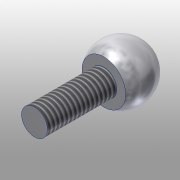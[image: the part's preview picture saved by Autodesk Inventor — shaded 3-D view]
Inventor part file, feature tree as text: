
AUTODESK INVENTOR PART (.ipt)
format: ipt  version: 2015 (Build 190159000, 159)  size: 129,024 bytes
history: native  units: mm
features: sketch x4, other x3
ambient origin geometry x8: Origin, YZ Plane, XZ Plane, XY Plane, X Axis, Y Axis, Z Axis, Center Point
bodies: Solid1 (feature_tree)
feature tree (7):
  other  "500-113.ipt"
  other  "Solid1::500-113.ipt"
  other  "TaggingFeature1"
  sketch  "Sketch1"  dims[d0=10.0mm]
  sketch  "Sketch2"
  sketch  "Sketch3"
  sketch  "Sketch4"
